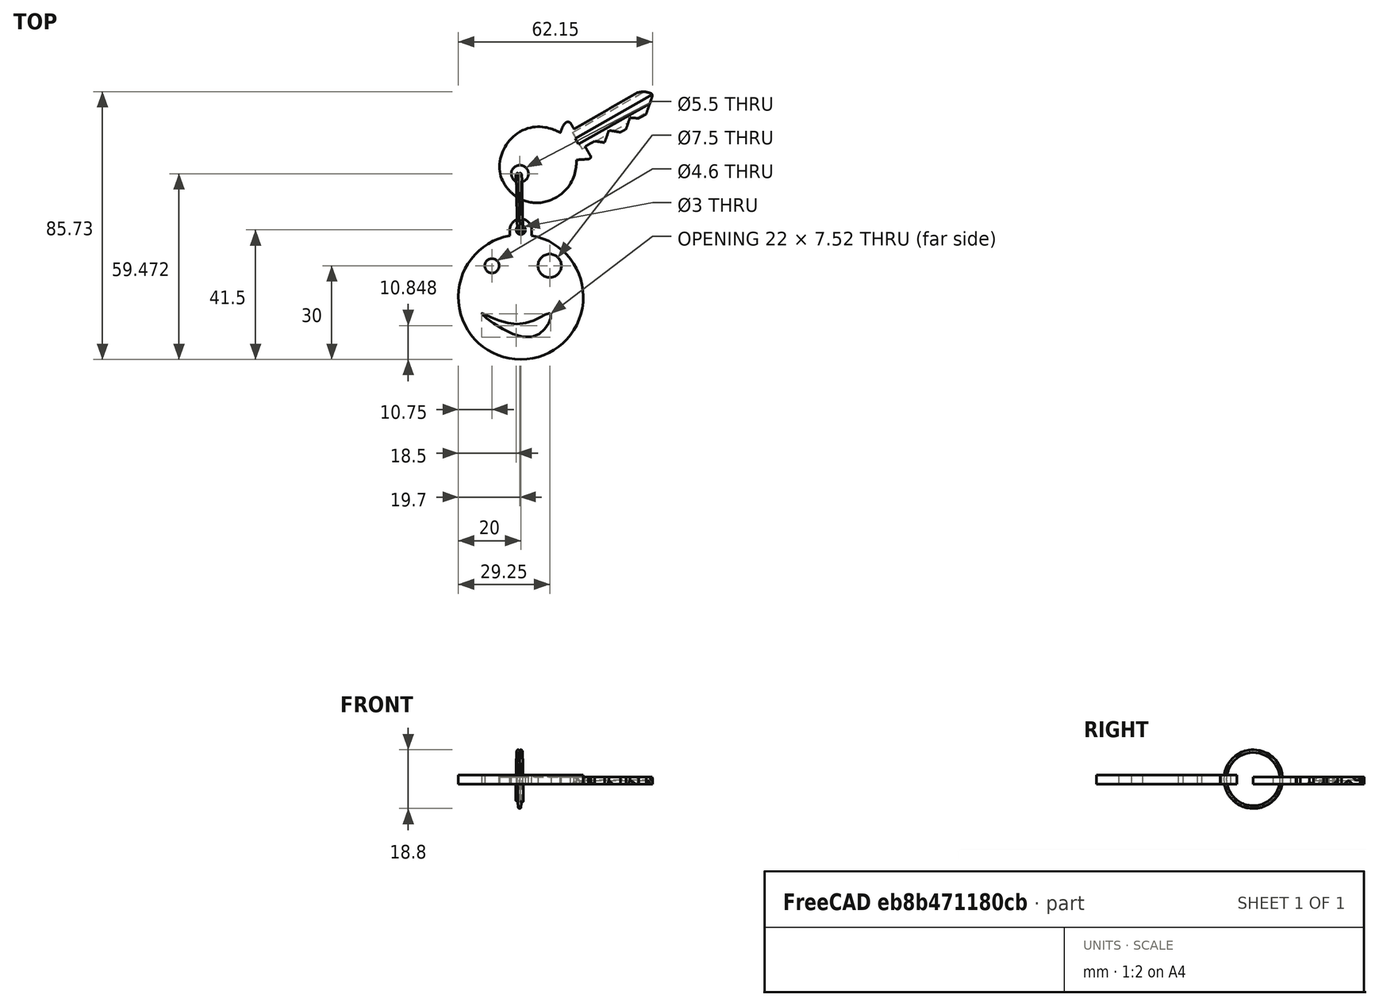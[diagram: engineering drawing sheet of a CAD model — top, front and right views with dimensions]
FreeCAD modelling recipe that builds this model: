
FCSTD DOCUMENT  (FreeCAD 0.18R16131 (Git))
Label: Llavero Smyle loco
License: CreativeCommons Attribution-ShareAlike
LicenseURL: http://creativecommons.org/licenses/by-sa/4.0/
objects: Part::Feature×2, App::DocumentObjectGroup×1, Sketcher::SketchObject×1, PartDesign::Pad×1, PartDesign::Body×1
note: 6 computed .brp shape members not serialized (recipe doc carries the construction recipe); baked Part::Feature solids carry a one-line shape summary decoded from their .brp

FEATURE [Part::Feature] Sweep  label="Anilla llaves"
  Placement = pos=(-1.2,30.2546,1.6391) rot=(0.333333,0.881918,0.333333;1.69612rad)
  shape: bbox 3.31 x 27.02 x 26.33 mm, 4 faces (baked)
FEATURE [Part::Feature] Cut  label="Llave"
  Placement = pos=(-5.46976,36.5266,0) rot=(0,0,1;0.517888rad)
  shape: bbox 49.82 x 36.6 x 2.3 mm, 44 faces (baked)
FEATURE [App::DocumentObjectGroup] Group  label="Assembly"
  Group = -> [Sweep,Cut]
FEATURE [Sketcher::SketchObject] Sketch  label="casino-chip-sketch"
  MapMode = 5
  Support = -> [XY_Plane]
  sketch-geometry (20):
    g0: Circle CenterX=1e-16 CenterY=21.5 CenterZ=0 NormalX=0 NormalY=0 NormalZ=1 AngleXU=0 Radius=1.5
    g1: LineSegment [constr] StartX=-3.5 StartY=21.5 StartZ=0 EndX=3.5 EndY=21.5 EndZ=0
    g2: ArcOfCircle CenterX=1e-16 CenterY=21.5 CenterZ=0 NormalX=0 NormalY=0 NormalZ=1 AngleXU=0 Radius=3.5 StartAngle=1e-16 EndAngle=3.14159
    g3: LineSegment StartX=-3.5 StartY=21.5 StartZ=0 EndX=-3.5 EndY=19.6914 EndZ=0
    g4: LineSegment [constr] StartX=-3.5 StartY=19.6914 StartZ=0 EndX=3.5 EndY=19.6914 EndZ=0
    g5: LineSegment StartX=3.5 StartY=19.6914 StartZ=0 EndX=3.5 EndY=21.5 EndZ=0
    g6: ArcOfCircle CenterX=0 CenterY=0 CenterZ=0 NormalX=0 NormalY=0 NormalZ=1 AngleXU=0 Radius=20 StartAngle=1.7467 EndAngle=7.67808
    g7: Circle CenterX=9.25 CenterY=10 CenterZ=0 NormalX=0 NormalY=0 NormalZ=1 AngleXU=0 Radius=3.75
    g8: Circle CenterX=-9.25 CenterY=10 CenterZ=0 NormalX=0 NormalY=0 NormalZ=1 AngleXU=0 Radius=2.3
    g9: LineSegment [constr] StartX=-9.25 StartY=10 StartZ=0 EndX=9.25 EndY=10 EndZ=0
    g10-g13: Circle [constr] x4 (B-spline internal-alignment scaffolding for g14; pole/knot coordinates omitted)
    g14: BSplineCurve PolesCount=4 KnotsCount=5 Degree=3 IsPeriodic=1
    g15-g19: GeomPoint [constr] x5 (B-spline internal-alignment scaffolding for g14; pole/knot coordinates omitted)
  constraints (41):
    c: Radius(g0) = 1.5
    c: Symmetric(g1,g1,g-2)
    c: Coincident(g2,g0)
    c: PointOnObject(g0,g1)
    c: Coincident(g2,g1)
    c: Coincident(g2,g1)
    c: Radius(g2) = 3.5
    c: DistanceY(g-1,g0) = 21.5
    c: Vertical(g3)
    c: Coincident(g3,g4)
    c: Horizontal(g4)
    c: Coincident(g4,g5)
    c: Vertical(g5)
    c: Coincident(g3,g1)
    c: Coincident(g5,g1)
    c: Coincident(g6,g-1)
    c: Radius(g6) = 20
    c: PointOnObject(g3,g6)
    c: PointOnObject(g6,g4)
    c: PointOnObject(g6,g4)
    c: Coincident(g9,g8)
    c: Coincident(g9,g7)
    c: Symmetric(g7,g8,g-2)
    c: DistanceX(g9,g9) = 18.5
    c: Radius(g7) = 3.75
    c: Radius(g8) = 2.3
    c: DistanceY(g6,g7) = 10
    c: Radius(g10) = 2
    c: Equal(g10,g11)
    c: Equal(g10,g12)
    c: Equal(g10,g13)
    c: InternalAlignment(g10-g13 -> g14) x4
    c: InternalAlignment(g15-g19 -> g14) x5
    c: PointOnObject(g10,g-1)
    c: PointOnObject(g10,g6)
    c: PointOnObject(g13,g6)
    c: PointOnObject(g11,g-2)
    c: PointOnObject(g12,g-1)
    c: DistanceX(g6,g12) = 13
    c: DistanceY(g11,g6) = 13
    c: DistanceX(g-1,g13) = 5
FEATURE [PartDesign::Pad] Pad
  Length = 3
  Length2 = 100
  Profile = -> Sketch
  Refine = true
  Type = 0
FEATURE [PartDesign::Body] Body  label="Llavero Smyle Loco"
  Group = -> [Sketch,Pad]
  Origin = -> Origin
  Tip = -> Pad
